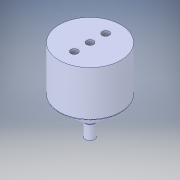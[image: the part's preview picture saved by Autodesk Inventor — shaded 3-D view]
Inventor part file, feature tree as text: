
AUTODESK INVENTOR PART (.ipt)
format: ipt  version: 2018 (Build 220112000, 112)  size: 279,552 bytes
history: native  units: in
note: dims shown in document units (in); Inventor stores cm internally (conversion verified against a paired STEP export)
features: sketch x9, extrude x8, other x4, fillet x3, loft x2, projected_geometry x2, plane x1, pattern_circular x1
ambient origin geometry x8: Origin, YZ Plane, XZ Plane, XY Plane, X Axis, Y Axis, Z Axis, Center Point
bodies: Solid1 (feature_tree)
feature tree (30):
  plane  "Work Plane1"
  sketch  "Sketch1"  dims[d0=0.3937in d1=0.0in d2=1.75in d3=0.0in]
  extrude  "Extrusion1"  Depth=1.75in TaperAngle=0.0deg
  extrude  "Extrusion2"  Depth=1.0in
  sketch  "Sketch2"  dims[d25=0.45in d26=1.0in]
  extrude  "Extrusion3"  Depth=0.25in
  sketch  "Sketch10"  dims[d35=0.5in d36=0.0in d37=0.0in d38=90.0deg]
  extrude  "Extrusion4"  TaperAngle=0.0deg  [1 undecoded]
  loft  "Loft2"
  loft  "Loft3"
  extrude  "Extrusion5"  Depth=0.481in
  fillet  "Fillet1"  Radius=0.0787in
  extrude  "Extrusion6"  Depth=0.25in TaperAngle=0.0deg
  pattern_circular  "Circular Pattern1"  Count=6  [1 undecoded]
  extrude  "Extrusion7"  Depth=0.25in TaperAngle=0.0deg
  extrude  "Extrusion8"  Depth=0.45in
  fillet  "Fillet2"  Radius=1.0in
  sketch  "Sketch9"  dims[d27=0.625in d28=0.0in d34=0.25in]
  projected_geometry  "Projected Loop7"
  projected_geometry  "Projected Loop8"
  sketch  "Sketch12"  dims[d39=0.0in d40=90.0deg d41=0.0in d42=90.0deg]
  other  "Edges2"
  other  "Edges3"
  other  "Edges4"
  other  "Edges5"
  sketch  "Sketch13"  dims[d43=0.0in d44=90.0deg d45=0.25in d46=0.0in]
  sketch  "Sketch14"  dims[d47=0.125in d49=0.481in d50=0.0787in]
  sketch  "Sketch16"  dims[d51=0.0394in d52=0.25in d53=0.0in d54=2.3622in d55=2.4737in]
  sketch  "Sketch17"  dims[d58=0.0591in d59=0.25in d60=0.0in d61=0.45in d62=1.0in d63=0.25in d64=0.0in d65=0.25in]
  fillet  "Fillet10"  Radius=0.25in
note: 2 required parameter values undecoded (feature->parameter linkage not recoverable at this tier; creation-order binding heuristic only, values carry confidence <= 0.55)
